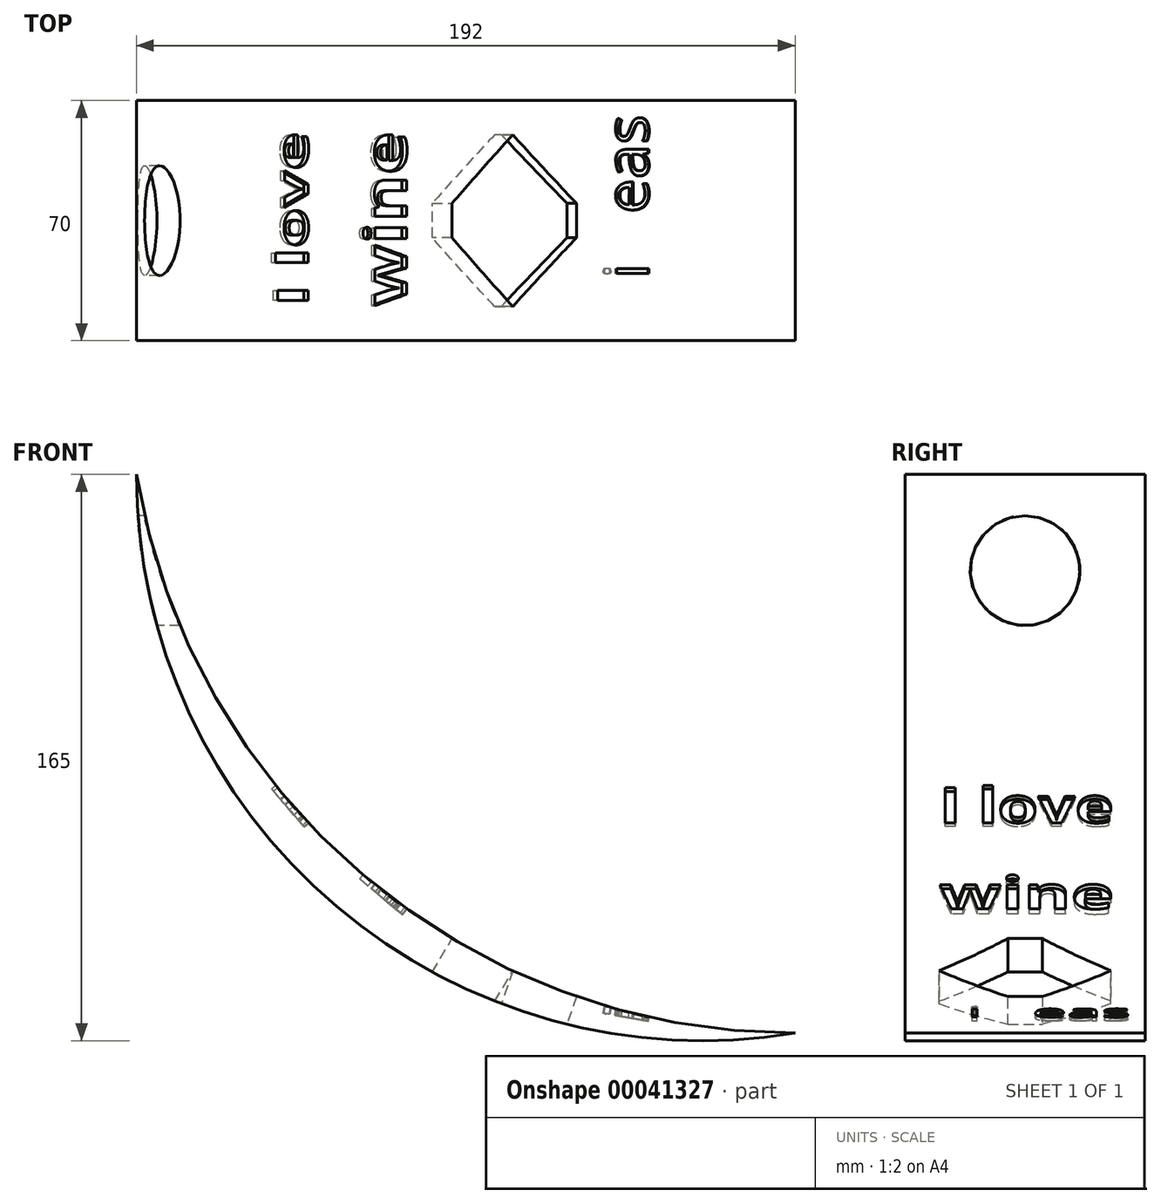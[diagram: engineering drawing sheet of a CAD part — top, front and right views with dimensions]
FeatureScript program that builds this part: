
annotation { "Feature Type Name" : "Feature", "Feature Type Description" : "" }
export const myFeature = defineFeature(function(context is Context, id is Id, definition is map)
    precondition{}
    {
        {
            var Q0;
            Q0=qCreatedBy(makeId("Front.planeOp"),FACE);
            var sketch = newSketch(context, id + "F0", { "sketchPlane" : qUnion([Q0])});
            skArc(sketch, "E0", {"start": v(0, 162.78) * mm, "mid": v(58.3, 36.92) * mm, "end": v(192, 0) * mm});
            skArc(sketch, "E1", {"start": v(0, 162.78) * mm, "mid": v(66.06, 46.07) * mm, "end": v(192, 0) * mm});
            skPoint(sketch, "E2", {"position": v(45.46, 66.35) * mm});
            skLineSegment(sketch, "E3", {"start": v(45.46, 66.35) * mm, "end": v(-27.34, 149.6) * mm, "construction": true});
            skPoint(sketch, "E4", {"position": v(66.9, 45.37) * mm});
            skLineSegment(sketch, "E5", {"start": v(66.9, 45.37) * mm, "end": v(118.52, 2.1) * mm, "construction": true});
            skPoint(sketch, "E6", {"position": v(158.06, 2.93) * mm});
            skLineSegment(sketch, "E7", {"start": v(158.06, 2.93) * mm, "end": v(233.86, -10.38) * mm, "construction": true});
            skSolve(sketch);
        }
        {
            var Q0;
            Q0 = qSketchRegion(id + "F0", true);
            extrude(context, id + "F1", {"entities" : qUnion([Q0]), "depth" : 70 * mm});
        }
        {
            var Q0;
            Q0=sQuery(id+"F0.wireOp",EDGE,"E3");
            cPlane(context, id + "F2", {"entities" : qUnion([Q0]), "cplaneType" : CPlaneType.LINE_ANGLE, "offset" : 150 * mm, "angle" : 0 * degree, "width" : 150 * mm, "height" : 150 * mm});
        }
        {
            var Q0;
            Q0=qCreatedBy(id+"F2.planeOp",FACE);
            var sketch = newSketch(context, id + "F3", { "sketchPlane" : qUnion([Q0])});
            skText(sketch, "E8", { "text": "I love", "fontName": "OpenSans-Bold.ttf"});
            skPoint(sketch, "E9", {"position": v(-60, 20.02) * mm});
            const initialGuessF3  = {"E8": [-0.06, 0.01318, 1, 0, 0.01368]};
            skSetInitialGuess(sketch, initialGuessF3);
            skSolve(sketch);
        }
        {
            var Q0;
            Q0 = qSketchRegion(id + "F3", true);
            extrude(context, id + "F4", {"entities" : qUnion([Q0]), "operationType" : NewBodyOperationType.REMOVE, "endBound" : BoundingType.SYMMETRIC, "oppositeDirection" : true, "depth" : 3 * mm});
        }
        {
            var Q0;
            Q0=qCreatedBy(makeId("Right.planeOp"),FACE);
            var sketch = newSketch(context, id + "F5", { "sketchPlane" : qUnion([Q0])});
            skCircle(sketch, "E10", {"center": v(-35, 134.78) * mm, "radius": 16 * mm});
            skPoint(sketch, "E11", {"position": v(-35, 162.78) * mm});
            skSolve(sketch);
        }
        {
            var Q0;
            Q0 = qSketchRegion(id + "F5", true);
            extrude(context, id + "F6", {"entities" : qUnion([Q0]), "operationType" : NewBodyOperationType.REMOVE, "depth" : 25 * mm});
        }
        {
            var Q0;
            Q0=sQuery(id+"F0.wireOp",EDGE,"E5");
            cPlane(context, id + "F7", {"entities" : qUnion([Q0]), "cplaneType" : CPlaneType.LINE_ANGLE, "offset" : 150 * mm, "angle" : 90 * degree, "width" : 150 * mm, "height" : 150 * mm});
        }
        {
            var Q0;
            Q0=qCreatedBy(id+"F7.planeOp",FACE);
            var sketch = newSketch(context, id + "F8", { "sketchPlane" : qUnion([Q0])});
            skText(sketch, "E12", { "text": "wine", "fontName": "OpenSans-Bold.ttf"});
            skPoint(sketch, "E13", {"position": v(22.13, -60) * mm});
            const initialGuessF8  = {"E12": [0.03706, -0.06, 0, 1, 0.01521]};
            skSetInitialGuess(sketch, initialGuessF8);
            skSolve(sketch);
        }
        {
            var Q0;
            Q0 = qSketchRegion(id + "F8", true);
            extrude(context, id + "F9", {"entities" : qUnion([Q0]), "operationType" : NewBodyOperationType.REMOVE, "endBound" : BoundingType.SYMMETRIC, "oppositeDirection" : true, "depth" : 3 * mm});
        }
        {
            var Q0;
            Q0=sQuery(id+"F0.wireOp",EDGE,"E7");
            cPlane(context, id + "F10", {"entities" : qUnion([Q0]), "cplaneType" : CPlaneType.LINE_ANGLE, "offset" : 150 * mm, "angle" : 90 * degree, "width" : 150 * mm, "height" : 150 * mm});
        }
        {
            var Q0;
            Q0=qCreatedBy(id+"F10.planeOp",FACE);
            var sketch = newSketch(context, id + "F11", { "sketchPlane" : qUnion([Q0])});
            skText(sketch, "E14", { "text": "3 D", "fontName": "OpenSans-Regular.ttf"});
            skPoint(sketch, "E15", {"position": v(155.17, -33.76) * mm});
            const initialGuessF11  = {"E14": [0.11078, -0.065, 0, 1, 0.015]};
            skSetInitialGuess(sketch, initialGuessF11);
            skSolve(sketch);
        }
        {
            var Q0;
            Q0 = qSketchRegion(id + "F11", true);
            extrude(context, id + "F12", {"entities" : qUnion([Q0]), "operationType" : NewBodyOperationType.ADD, "depth" : 2 * mm});
        }
        {
            var Q0;
            Q0=qCreatedBy(id+"F10.planeOp",FACE);
            var sketch = newSketch(context, id + "F13", { "sketchPlane" : qUnion([Q0])});
            skText(sketch, "E16", { "text": "i", "fontName": "OpenSans-Regular.ttf"});
            skText(sketch, "E17", { "text": "eas", "fontName": "OpenSans-Regular.ttf"});
            const initialGuessF13  = {"E16": [0.14624, -0.052, 0, 1, 0.013], "E17": [0.14624, -0.03296, 0, 1, 0.013]};
            skSetInitialGuess(sketch, initialGuessF13);
            skSolve(sketch);
        }
        {
            var Q0;
            Q0 = qSketchRegion(id + "F13", true);
            extrude(context, id + "F14", {"entities" : qUnion([Q0]), "operationType" : NewBodyOperationType.REMOVE, "endBound" : BoundingType.SYMMETRIC, "oppositeDirection" : true, "depth" : 2 * mm});
        }
        {
            var Q0;
            {var subQ0=sQuery(id+"F0.wireOp",EDGE,"E0");var subQ1=sQuery(id+"F0.wireOp",EDGE,"E1");Q0=makeQuery(id+"F1.opExtrude","SWEPT_EDGE",EDGE,{"disambiguationData":[OSD([subQ0,subQ1]),TDD([makeQuery(id+"F0.imprint","INTERSECT",VERTEX,{"disambiguationData":[OD(0.0)],"derivedFrom":[subQ0,subQ1]})])]});}
            cPlane(context, id + "F15", {"entities" : qUnion([Q0]), "cplaneType" : CPlaneType.MID_PLANE, "offset" : 150 * mm, "width" : 150 * mm, "height" : 150 * mm});
        }
        {
            var Q0;
            Q0=qCreatedBy(id+"F15.planeOp",FACE);
            var sketch = newSketch(context, id + "F16", { "sketchPlane" : qUnion([Q0])});
            skArc(sketch, "E18", {"start": v(-128.25, 10.64) * mm, "mid": v(-109.68, 18.14) * mm, "end": v(-91.99, 27.52) * mm});
            skArc(sketch, "E19", {"start": v(-125.47, 2.58) * mm, "mid": v(-105.34, 8.94) * mm, "end": v(-86.19, 17.82) * mm});
            skLineSegment(sketch, "E20", {"start": v(-91.99, 27.52) * mm, "end": v(-86.19, 17.82) * mm});
            skLineSegment(sketch, "E21", {"start": v(-128.25, 10.64) * mm, "end": v(-125.47, 2.58) * mm});
            skPoint(sketch, "E22", {"position": v(-109.68, 18.14) * mm});
            skLineSegment(sketch, "E23", {"start": v(-66.9, 45.37) * mm, "end": v(-158.06, 2.93) * mm, "construction": true});
            skPoint(sketch, "E24", {"position": v(-112.48, 24.15) * mm});
            skLineSegment(sketch, "E25", {"start": v(-112.48, 24.15) * mm, "end": v(-109.68, 18.14) * mm, "construction": true});
            skSolve(sketch);
        }
        {
            var Q0;
            Q0 = qSketchRegion(id + "F16", true);
            extrude(context, id + "F17", {"entities" : qUnion([Q0]), "operationType" : NewBodyOperationType.REMOVE, "endBound" : BoundingType.SYMMETRIC, "oppositeDirection" : true, "depth" : 50 * mm});
        }
        {
            var Q0;
            Q0=makeQuery(id+"F17.boolean.opBoolean","COPY",EDGE,{"derivedFrom":makeQuery(id+"F17.opExtrude","CAP_EDGE",EDGE,{"disambiguationData":[OSD([sQuery(id+"F16.wireOp",EDGE,"E20")])],"isStart":true})});
            var Q1;
            Q1=makeQuery(id+"F17.boolean.opBoolean","COPY",EDGE,{"derivedFrom":makeQuery(id+"F17.opExtrude","CAP_EDGE",EDGE,{"disambiguationData":[OSD([sQuery(id+"F16.wireOp",EDGE,"E20")])],"isStart":false})});
            var Q2;
            Q2=makeQuery(id+"F17.boolean.opBoolean","COPY",EDGE,{"derivedFrom":makeQuery(id+"F17.opExtrude","CAP_EDGE",EDGE,{"disambiguationData":[OSD([sQuery(id+"F16.wireOp",EDGE,"E21")])],"isStart":false})});
            var Q3;
            Q3=makeQuery(id+"F17.boolean.opBoolean","COPY",EDGE,{"derivedFrom":makeQuery(id+"F17.opExtrude","CAP_EDGE",EDGE,{"disambiguationData":[OSD([sQuery(id+"F16.wireOp",EDGE,"E21")])],"isStart":true})});
            chamfer(context, id + "F18", {"entities" : qUnion([Q0, Q1, Q2, Q3]), "width" : 20 * mm, "tangentPropagation" : true});
        }
    });
